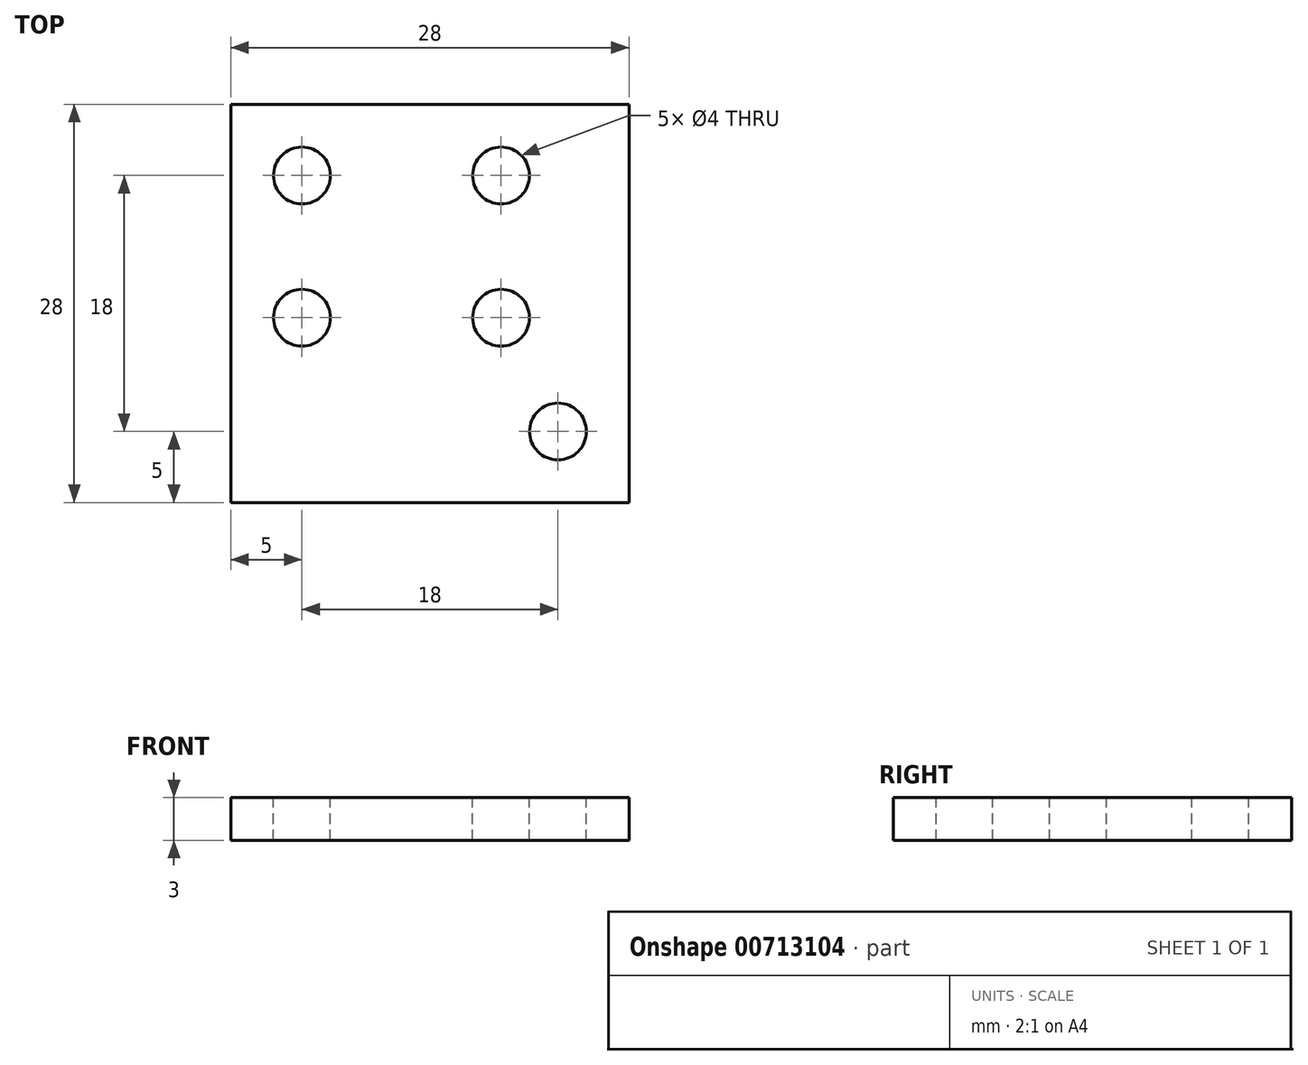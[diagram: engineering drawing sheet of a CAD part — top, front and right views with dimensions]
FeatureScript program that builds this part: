
annotation { "Feature Type Name" : "Feature", "Feature Type Description" : "" }
export const myFeature = defineFeature(function(context is Context, id is Id, definition is map)
    precondition{}
    {
        {
            var Q0;
            Q0=qCreatedBy(makeId("Top.planeOp"),FACE);
            var sketch = newSketch(context, id + "F0", { "sketchPlane" : qUnion([Q0])});
            skLineSegment(sketch, "E0.bottom", {"start": v(19, -19) * mm, "end": v(-19, -19) * mm});
            skLineSegment(sketch, "E0.top", {"start": v(19, 19) * mm, "end": v(-19, 19) * mm});
            skLineSegment(sketch, "E0.left", {"start": v(19, -19) * mm, "end": v(19, 19) * mm});
            skLineSegment(sketch, "E0.right", {"start": v(-19, -19) * mm, "end": v(-19, 19) * mm});
            skPoint(sketch, "E0.middle", {"position": v(0, 0) * mm});
            skSolve(sketch);
        }
        {
            var Q0;
            Q0=makeQuery(id+"F0.imprint","IMPRINT",FACE,{"disambiguationData":[TD([[makeQuery(id+"F0.imprint","IMPRINT",EDGE,{"derivedFrom":sQuery(id+"F0.wireOp",EDGE,"E0.bottom")}),-1.0]])]});
            extrude(context, id + "F1", {"entities" : qUnion([Q0]), "depth" : 3 * mm, "offsetDistance" : 25 * mm});
        }
        {
            var Q0;
            Q0=makeQuery(id+"F1.opExtrude","CAP_FACE",FACE,{"disambiguationData":[OSD([sQuery(id+"F0.wireOp",EDGE,"E0.bottom"),sQuery(id+"F0.wireOp",EDGE,"E0.top"),sQuery(id+"F0.wireOp",EDGE,"E0.left"),sQuery(id+"F0.wireOp",EDGE,"E0.right")])],"isStart":false});
            var sketch = newSketch(context, id + "F2", { "sketchPlane" : qUnion([Q0])});
            skLineSegment(sketch, "E1.right", {"start": v(-14, 4) * mm, "end": v(-14, 14) * mm});
            skLineSegment(sketch, "E2", {"start": v(0, 14) * mm, "end": v(0, 4) * mm});
            skPoint(sketch, "E3", {"position": v(4, -4) * mm});
            skSolve(sketch);
        }
        {
            var Q0;
            Q0=sQuery(id+"F2.wireOp",VERTEX,"E2.end");
            var Q1;
            Q1=sQuery(id+"F2.wireOp",VERTEX,"E2.start");
            var Q2;
            Q2=sQuery(id+"F2.wireOp",VERTEX,"E1.right.end");
            var Q3;
            Q3=sQuery(id+"F2.wireOp",VERTEX,"E3");
            var Q4;
            Q4=sQuery(id+"F2.wireOp",VERTEX,"E1.right.start");
            var Q5;
            Q5=makeQuery(id+"F1.opExtrude","SWEPT_BODY",BODY,{"disambiguationData":[OSD([sQuery(id+"F0.wireOp",EDGE,"E0.bottom"),sQuery(id+"F0.wireOp",EDGE,"E0.top"),sQuery(id+"F0.wireOp",EDGE,"E0.left"),sQuery(id+"F0.wireOp",EDGE,"E0.right")])]});
            hole(context, id + "F3", {"style" : HoleStyle.SIMPLE, "endStyle" : HoleEndStyle.THROUGH, "holeDiameter" : 4 * mm, "majorDiameter" : 5 * mm, "isTappedThrough" : true, "tappedDepth" : 12 * mm, "tapClearance" : 3, "locations" : qUnion([Q0, Q1, Q2, Q3, Q4]), "scope" : qUnion([Q5])});
        }
        {
            var Q0;
            Q0=makeQuery(id+"F1.opExtrude","CAP_FACE",FACE,{"disambiguationData":[OSD([sQuery(id+"F0.wireOp",EDGE,"E0.bottom"),sQuery(id+"F0.wireOp",EDGE,"E0.top"),sQuery(id+"F0.wireOp",EDGE,"E0.left"),sQuery(id+"F0.wireOp",EDGE,"E0.right")])],"isStart":false});
            var sketch = newSketch(context, id + "F4", { "sketchPlane" : qUnion([Q0])});
            skLineSegment(sketch, "E4.bottom", {"start": v(-19, 19) * mm, "end": v(9, 19) * mm});
            skLineSegment(sketch, "E4.top", {"start": v(-19, -9) * mm, "end": v(9, -9) * mm});
            skLineSegment(sketch, "E4.left", {"start": v(-19, 19) * mm, "end": v(-19, -9) * mm});
            skLineSegment(sketch, "E4.right", {"start": v(9, 19) * mm, "end": v(9, -9) * mm});
            skSolve(sketch);
        }
        {
            var Q0;
            {var subQ4=sQuery(id+"F4.wireOp",EDGE,"E4.top");Q0=makeQuery(id+"F4.imprint","IMPRINT",FACE,{"disambiguationData":[TD([[makeQuery(id+"F4.imprint","IMPRINT",EDGE,{"derivedFrom":subQ4}),-1.0]])]});}
            extrude(context, id + "F5", {"entities" : qUnion([Q0]), "operationType" : NewBodyOperationType.REMOVE, "oppositeDirection" : true, "depth" : 25 * mm, "offsetDistance" : 25 * mm});
        }
    });
